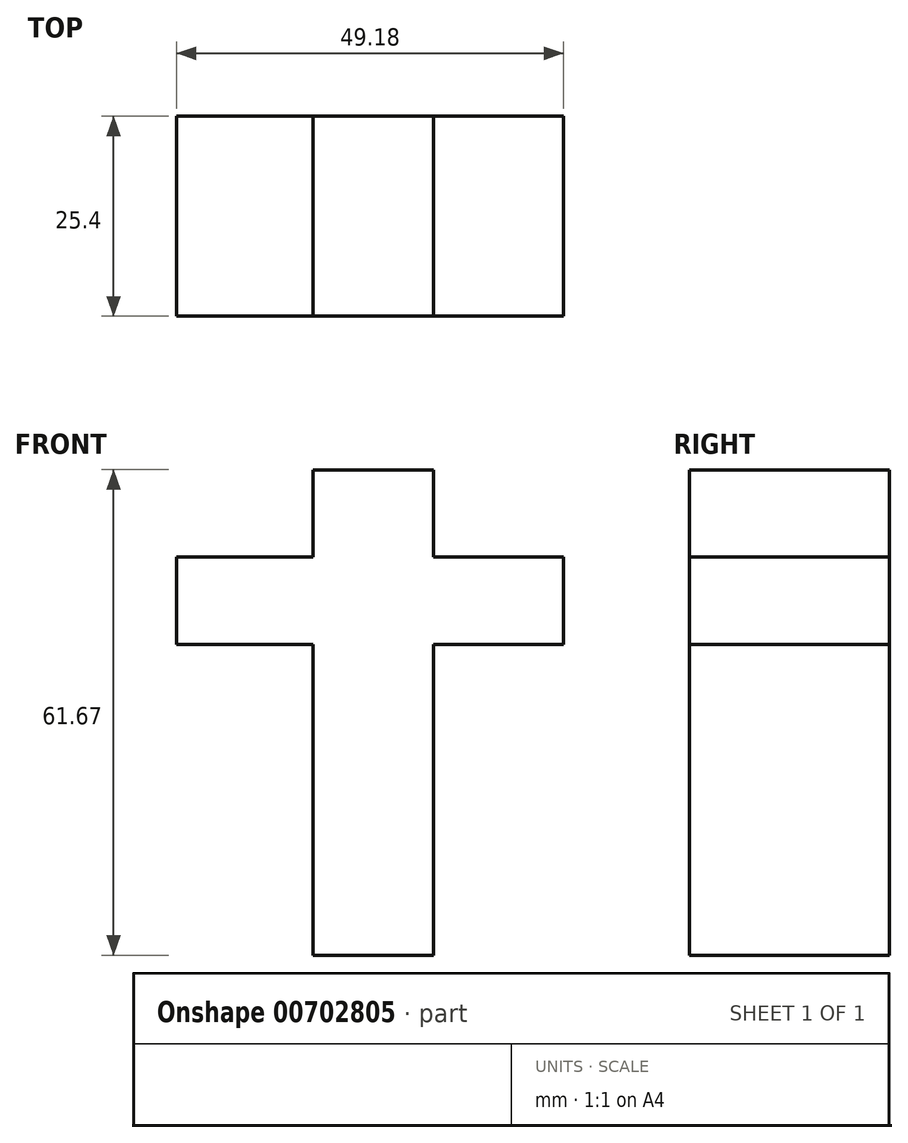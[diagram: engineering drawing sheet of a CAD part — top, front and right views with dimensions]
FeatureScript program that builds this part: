
annotation { "Feature Type Name" : "Feature", "Feature Type Description" : "" }
export const myFeature = defineFeature(function(context is Context, id is Id, definition is map)
    precondition{}
    {
        {
            var Q0;
            Q0=qCreatedBy(makeId("Front.planeOp"),FACE);
            var sketch = newSketch(context, id + "F0", { "sketchPlane" : qUnion([Q0])});
            skLineSegment(sketch, "E0", {"start": v(-44.04, 50.69) * mm, "end": v(-44.04, 11.19) * mm});
            skLineSegment(sketch, "E1", {"start": v(-44.04, 50.69) * mm, "end": v(-61.37, 50.69) * mm});
            skLineSegment(sketch, "E2", {"start": v(-61.37, 50.69) * mm, "end": v(-61.37, 61.77) * mm});
            skLineSegment(sketch, "E3", {"start": v(-61.37, 61.77) * mm, "end": v(-44.04, 61.77) * mm});
            skLineSegment(sketch, "E4", {"start": v(-44.04, 61.77) * mm, "end": v(-44.04, 72.86) * mm});
            skLineSegment(sketch, "E5", {"start": v(-44.04, 72.86) * mm, "end": v(-28.72, 72.86) * mm});
            skLineSegment(sketch, "E6", {"start": v(-28.72, 72.86) * mm, "end": v(-28.72, 61.77) * mm});
            skLineSegment(sketch, "E7", {"start": v(-28.72, 61.77) * mm, "end": v(-12.2, 61.77) * mm});
            skLineSegment(sketch, "E8", {"start": v(-12.2, 61.77) * mm, "end": v(-12.2, 50.69) * mm});
            skLineSegment(sketch, "E9", {"start": v(-12.2, 50.69) * mm, "end": v(-28.72, 50.69) * mm});
            skLineSegment(sketch, "E10", {"start": v(-28.72, 50.69) * mm, "end": v(-28.72, 11.19) * mm});
            skLineSegment(sketch, "E11", {"start": v(-28.72, 11.19) * mm, "end": v(-44.04, 11.19) * mm});
            skSolve(sketch);
        }
        {
            var Q0;
            Q0=makeQuery(id+"F0.imprint","IMPRINT",FACE,{"disambiguationData":[TD([[makeQuery(id+"F0.imprint","IMPRINT",EDGE,{"derivedFrom":sQuery(id+"F0.wireOp",EDGE,"E0")}),1.0]])]});
            extrude(context, id + "F1", {"entities" : qUnion([Q0]), "depth" : 25.4 * mm, "offsetDistance" : 25.4 * mm});
        }
    });
